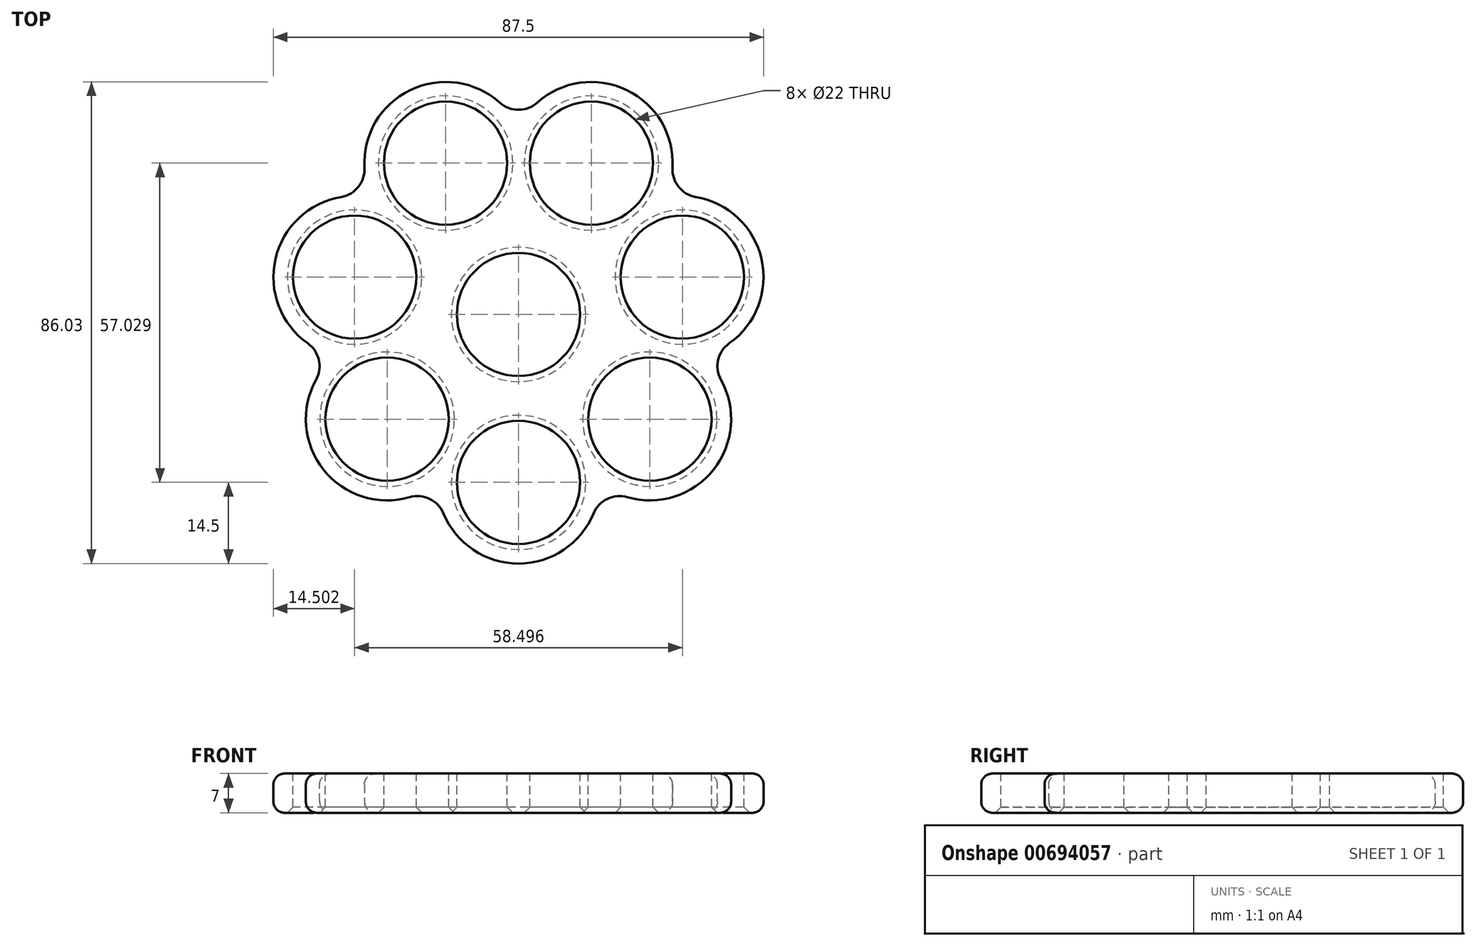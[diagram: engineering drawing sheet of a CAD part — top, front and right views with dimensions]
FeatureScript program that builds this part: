
annotation { "Feature Type Name" : "Feature", "Feature Type Description" : "" }
export const myFeature = defineFeature(function(context is Context, id is Id, definition is map)
    precondition{}
    {
        {
            var Q0;
            Q0=qCreatedBy(makeId("Top.planeOp"),FACE);
            var sketch = newSketch(context, id + "F0", { "sketchPlane" : qUnion([Q0])});
            skCircle(sketch, "E0", {"center": v(0, 0) * mm, "radius": 14.5 * mm});
            skCircle(sketch, "E1", {"center": v(0, -30) * mm, "radius": 14.5 * mm});
            skLineSegment(sketch, "E2", {"start": v(14.5, 0) * mm, "end": v(14.5, -30) * mm});
            skLineSegment(sketch, "E3", {"start": v(-14.5, 0) * mm, "end": v(-14.5, -30) * mm});
            skSolve(sketch);
        }
        {
            var Q0;
            Q0=qSketchRegion(id+"F0",true);
            var Q1;
            {var subQ0=sQuery(id+"F0.wireOp",EDGE,"E1");var subQ1=sQuery(id+"F0.wireOp",EDGE,"E0");var subQ2=makeQuery(id+"F0.imprint","INTERSECT",VERTEX,{"disambiguationData":[OD(0.0)],"derivedFrom":[subQ1,subQ0]});Q1=makeQuery(id+"F0.imprint","IMPRINT",FACE,{"disambiguationData":[TD([[makeQuery(id+"F0.imprint","IMPRINT",EDGE,{"disambiguationData":[TD([[subQ2,-1.0]])],"derivedFrom":subQ1}),1.0]])]});}
            extrude(context, id + "F1", {"entities" : qUnion([Q0, Q1]), "depth" : 7 * mm, "offsetDistance" : 25 * mm});
        }
        {
            var Q0;
            Q0=qCreatedBy(makeId("Front.planeOp"),FACE);
            var sketch = newSketch(context, id + "F2", { "sketchPlane" : qUnion([Q0])});
            skLineSegment(sketch, "E4", {"start": v(0, 0) * mm, "end": v(0, 26.48) * mm});
            skSolve(sketch);
        }
        {
            var Q0;
            Q0=makeQuery(id+"F1.opExtrude","SWEPT_BODY",BODY,{"disambiguationData":[OSD([sQuery(id+"F0.wireOp",EDGE,"E0"),sQuery(id+"F0.wireOp",EDGE,"E1"),sQuery(id+"F0.wireOp",EDGE,"E2"),sQuery(id+"F0.wireOp",EDGE,"E3")])]});
            var Q1;
            Q1=sQuery(id+"F2.wireOp",EDGE,"E4");
            circularPattern(context, id + "F3", {"entities" : qUnion([Q0]), "axis" : qUnion([Q1]), "angle" : 360 * degree, "instanceCount" : 7, "equalSpace" : true});
        }
        {
            var Q0;
            Q0=makeQuery(id+"F3.opPattern","COPY",BODY,{"derivedFrom":makeQuery(id+"F1.opExtrude","SWEPT_BODY",BODY,{"disambiguationData":[OSD([sQuery(id+"F0.wireOp",EDGE,"E0"),sQuery(id+"F0.wireOp",EDGE,"E1"),sQuery(id+"F0.wireOp",EDGE,"E2"),sQuery(id+"F0.wireOp",EDGE,"E3")])]}),"instanceName":"5"});
            var Q1;
            Q1=makeQuery(id+"F3.opPattern","COPY",BODY,{"derivedFrom":makeQuery(id+"F1.opExtrude","SWEPT_BODY",BODY,{"disambiguationData":[OSD([sQuery(id+"F0.wireOp",EDGE,"E0"),sQuery(id+"F0.wireOp",EDGE,"E1"),sQuery(id+"F0.wireOp",EDGE,"E2"),sQuery(id+"F0.wireOp",EDGE,"E3")])]}),"instanceName":"6"});
            var Q2;
            Q2=makeQuery(id+"F1.opExtrude","SWEPT_BODY",BODY,{"disambiguationData":[OSD([sQuery(id+"F0.wireOp",EDGE,"E0"),sQuery(id+"F0.wireOp",EDGE,"E1"),sQuery(id+"F0.wireOp",EDGE,"E2"),sQuery(id+"F0.wireOp",EDGE,"E3")])]});
            var Q3;
            Q3=makeQuery(id+"F3.opPattern","COPY",BODY,{"derivedFrom":makeQuery(id+"F1.opExtrude","SWEPT_BODY",BODY,{"disambiguationData":[OSD([sQuery(id+"F0.wireOp",EDGE,"E0"),sQuery(id+"F0.wireOp",EDGE,"E1"),sQuery(id+"F0.wireOp",EDGE,"E2"),sQuery(id+"F0.wireOp",EDGE,"E3")])]}),"instanceName":"1"});
            var Q4;
            Q4=makeQuery(id+"F3.opPattern","COPY",BODY,{"derivedFrom":makeQuery(id+"F1.opExtrude","SWEPT_BODY",BODY,{"disambiguationData":[OSD([sQuery(id+"F0.wireOp",EDGE,"E0"),sQuery(id+"F0.wireOp",EDGE,"E1"),sQuery(id+"F0.wireOp",EDGE,"E2"),sQuery(id+"F0.wireOp",EDGE,"E3")])]}),"instanceName":"2"});
            var Q5;
            Q5=makeQuery(id+"F3.opPattern","COPY",BODY,{"derivedFrom":makeQuery(id+"F1.opExtrude","SWEPT_BODY",BODY,{"disambiguationData":[OSD([sQuery(id+"F0.wireOp",EDGE,"E0"),sQuery(id+"F0.wireOp",EDGE,"E1"),sQuery(id+"F0.wireOp",EDGE,"E2"),sQuery(id+"F0.wireOp",EDGE,"E3")])]}),"instanceName":"3"});
            var Q6;
            Q6=makeQuery(id+"F3.opPattern","COPY",BODY,{"derivedFrom":makeQuery(id+"F1.opExtrude","SWEPT_BODY",BODY,{"disambiguationData":[OSD([sQuery(id+"F0.wireOp",EDGE,"E0"),sQuery(id+"F0.wireOp",EDGE,"E1"),sQuery(id+"F0.wireOp",EDGE,"E2"),sQuery(id+"F0.wireOp",EDGE,"E3")])]}),"instanceName":"4"});
            booleanBodies(context, id + "F4", {"operationType" : BooleanOperationType.UNION, "tools" : qUnion([Q0, Q1, Q2, Q3, Q4, Q5, Q6])});
        }
        {
            var Q0;
            Q0=makeQuery(id+"F1.opExtrude","CAP_FACE",FACE,{"disambiguationData":[OSD([sQuery(id+"F0.wireOp",EDGE,"E0"),sQuery(id+"F0.wireOp",EDGE,"E1"),sQuery(id+"F0.wireOp",EDGE,"E2"),sQuery(id+"F0.wireOp",EDGE,"E3")])],"isStart":false});
            var sketch = newSketch(context, id + "F5", { "sketchPlane" : qUnion([Q0])});
            skCircle(sketch, "E5", {"center": v(0, 0) * mm, "radius": 11 * mm});
            skCircle(sketch, "E6", {"center": v(0, -30) * mm, "radius": 11 * mm});
            skLineSegment(sketch, "E7", {"start": v(0, 0) * mm, "end": v(0, -30) * mm});
            skCircle(sketch, "E8.1.0", {"center": v(23.45, -18.7) * mm, "radius": 11 * mm});
            skCircle(sketch, "E8.2.0", {"center": v(29.25, 6.68) * mm, "radius": 11 * mm});
            skCircle(sketch, "E8.3.0", {"center": v(13.02, 27.03) * mm, "radius": 11 * mm});
            skCircle(sketch, "E8.4.0", {"center": v(-13.02, 27.03) * mm, "radius": 11 * mm});
            skCircle(sketch, "E8.5.0", {"center": v(-29.25, 6.68) * mm, "radius": 11 * mm});
            skCircle(sketch, "E8.6.0", {"center": v(-23.45, -18.7) * mm, "radius": 11 * mm});
            skSolve(sketch);
        }
        {
            var Q0;
            Q0=qSketchRegion(id+"F5",true);
            extrude(context, id + "F6", {"entities" : qUnion([Q0]), "operationType" : NewBodyOperationType.REMOVE, "endBound" : BoundingType.THROUGH_ALL, "oppositeDirection" : true, "depth" : 25 * mm, "offsetDistance" : 25 * mm});
        }
        {
            var Q0;
            {var subQ0=makeQuery(id+"F1.opExtrude","SWEPT_FACE",FACE,{"disambiguationData":[OSD([sQuery(id+"F0.wireOp",EDGE,"E1")])]});Q0=makeQuery(id+"F4.opBoolean","INTERSECT",EDGE,{"derivedFrom":[makeQuery(id+"F3.opPattern","COPY",FACE,{"derivedFrom":subQ0,"instanceName":"4"}),makeQuery(id+"F3.opPattern","COPY",FACE,{"derivedFrom":subQ0,"instanceName":"5"})]});}
            var Q1;
            {var subQ0=makeQuery(id+"F1.opExtrude","SWEPT_FACE",FACE,{"disambiguationData":[OSD([sQuery(id+"F0.wireOp",EDGE,"E1")])]});Q1=makeQuery(id+"F4.opBoolean","INTERSECT",EDGE,{"derivedFrom":[makeQuery(id+"F3.opPattern","COPY",FACE,{"derivedFrom":subQ0,"instanceName":"5"}),makeQuery(id+"F3.opPattern","COPY",FACE,{"derivedFrom":subQ0,"instanceName":"6"})]});}
            var Q2;
            {var subQ0=makeQuery(id+"F1.opExtrude","SWEPT_FACE",FACE,{"disambiguationData":[OSD([sQuery(id+"F0.wireOp",EDGE,"E1")])]});Q2=makeQuery(id+"F4.opBoolean","INTERSECT",EDGE,{"derivedFrom":[subQ0,makeQuery(id+"F3.opPattern","COPY",FACE,{"derivedFrom":subQ0,"instanceName":"6"})]});}
            var Q3;
            {var subQ0=makeQuery(id+"F1.opExtrude","SWEPT_FACE",FACE,{"disambiguationData":[OSD([sQuery(id+"F0.wireOp",EDGE,"E1")])]});Q3=makeQuery(id+"F4.opBoolean","INTERSECT",EDGE,{"derivedFrom":[subQ0,makeQuery(id+"F3.opPattern","COPY",FACE,{"derivedFrom":subQ0,"instanceName":"1"})]});}
            var Q4;
            {var subQ0=makeQuery(id+"F1.opExtrude","SWEPT_FACE",FACE,{"disambiguationData":[OSD([sQuery(id+"F0.wireOp",EDGE,"E1")])]});Q4=makeQuery(id+"F4.opBoolean","INTERSECT",EDGE,{"derivedFrom":[makeQuery(id+"F3.opPattern","COPY",FACE,{"derivedFrom":subQ0,"instanceName":"1"}),makeQuery(id+"F3.opPattern","COPY",FACE,{"derivedFrom":subQ0,"instanceName":"2"})]});}
            var Q5;
            {var subQ0=makeQuery(id+"F1.opExtrude","SWEPT_FACE",FACE,{"disambiguationData":[OSD([sQuery(id+"F0.wireOp",EDGE,"E1")])]});Q5=makeQuery(id+"F4.opBoolean","INTERSECT",EDGE,{"derivedFrom":[makeQuery(id+"F3.opPattern","COPY",FACE,{"derivedFrom":subQ0,"instanceName":"2"}),makeQuery(id+"F3.opPattern","COPY",FACE,{"derivedFrom":subQ0,"instanceName":"3"})]});}
            var Q6;
            {var subQ0=makeQuery(id+"F1.opExtrude","SWEPT_FACE",FACE,{"disambiguationData":[OSD([sQuery(id+"F0.wireOp",EDGE,"E1")])]});Q6=makeQuery(id+"F4.opBoolean","INTERSECT",EDGE,{"derivedFrom":[makeQuery(id+"F3.opPattern","COPY",FACE,{"derivedFrom":subQ0,"instanceName":"3"}),makeQuery(id+"F3.opPattern","COPY",FACE,{"derivedFrom":subQ0,"instanceName":"4"})]});}
            fillet(context, id + "F7", {"entities" : qUnion([Q0, Q1, Q2, Q3, Q4, Q5, Q6]), "radius" : 5 * mm, "tangentPropagation" : true, "allowEdgeOverflow" : false});
        }
        {
            var Q0;
            Q0=makeQuery(id+"F3.opPattern","COPY",EDGE,{"derivedFrom":makeQuery(id+"F1.opExtrude","CAP_EDGE",EDGE,{"disambiguationData":[OSD([sQuery(id+"F0.wireOp",EDGE,"E1")])],"isStart":false}),"instanceName":"1"});
            var Q1;
            Q1=makeQuery(id+"F1.opExtrude","CAP_EDGE",EDGE,{"disambiguationData":[OSD([sQuery(id+"F0.wireOp",EDGE,"E1")])],"isStart":true});
            fillet(context, id + "F8", {"entities" : qUnion([Q0, Q1]), "radius" : 2 * mm, "tangentPropagation" : true, "allowEdgeOverflow" : false});
        }
        {
            var Q0;
            Q0=makeQuery(id+"F3.opPattern","COPY",EDGE,{"derivedFrom":makeQuery(id+"F6.boolean.opBoolean","COPY",EDGE,{"derivedFrom":makeQuery(id+"F6.opExtrude","CAP_EDGE",EDGE,{"disambiguationData":[OSD([sQuery(id+"F5.wireOp",EDGE,"E5")])],"isStart":true})}),"instanceName":"4"});
            var Q1;
            Q1=makeQuery(id+"F3.opPattern","COPY",EDGE,{"derivedFrom":makeQuery(id+"F6.boolean.opBoolean","COPY",EDGE,{"derivedFrom":makeQuery(id+"F6.opExtrude","CAP_EDGE",EDGE,{"disambiguationData":[OSD([sQuery(id+"F5.wireOp",EDGE,"E6")])],"isStart":true})}),"instanceName":"2"});
            var Q2;
            Q2=makeQuery(id+"F3.opPattern","COPY",EDGE,{"derivedFrom":makeQuery(id+"F6.boolean.opBoolean","COPY",EDGE,{"derivedFrom":makeQuery(id+"F6.opExtrude","CAP_EDGE",EDGE,{"disambiguationData":[OSD([sQuery(id+"F5.wireOp",EDGE,"E6")])],"isStart":true})}),"instanceName":"3"});
            var Q3;
            Q3=makeQuery(id+"F3.opPattern","COPY",EDGE,{"derivedFrom":makeQuery(id+"F6.boolean.opBoolean","COPY",EDGE,{"derivedFrom":makeQuery(id+"F6.opExtrude","CAP_EDGE",EDGE,{"disambiguationData":[OSD([sQuery(id+"F5.wireOp",EDGE,"E6")])],"isStart":true})}),"instanceName":"4"});
            var Q4;
            Q4=makeQuery(id+"F3.opPattern","COPY",EDGE,{"derivedFrom":makeQuery(id+"F6.boolean.opBoolean","COPY",EDGE,{"derivedFrom":makeQuery(id+"F6.opExtrude","CAP_EDGE",EDGE,{"disambiguationData":[OSD([sQuery(id+"F5.wireOp",EDGE,"E6")])],"isStart":true})}),"instanceName":"5"});
            var Q5;
            Q5=makeQuery(id+"F6.boolean.opBoolean","COPY",EDGE,{"derivedFrom":makeQuery(id+"F6.opExtrude","CAP_EDGE",EDGE,{"disambiguationData":[OSD([sQuery(id+"F5.wireOp",EDGE,"E6")])],"isStart":true})});
            var Q6;
            Q6=makeQuery(id+"F3.opPattern","COPY",EDGE,{"derivedFrom":makeQuery(id+"F6.boolean.opBoolean","COPY",EDGE,{"derivedFrom":makeQuery(id+"F6.opExtrude","CAP_EDGE",EDGE,{"disambiguationData":[OSD([sQuery(id+"F5.wireOp",EDGE,"E6")])],"isStart":true})}),"instanceName":"1"});
            var Q7;
            Q7=makeQuery(id+"F3.opPattern","COPY",EDGE,{"derivedFrom":makeQuery(id+"F6.boolean.opBoolean","INTERSECT",EDGE,{"derivedFrom":[makeQuery(id+"F1.opExtrude","CAP_FACE",FACE,{"disambiguationData":[OSD([sQuery(id+"F0.wireOp",EDGE,"E0"),sQuery(id+"F0.wireOp",EDGE,"E1"),sQuery(id+"F0.wireOp",EDGE,"E2"),sQuery(id+"F0.wireOp",EDGE,"E3")])],"isStart":true}),makeQuery(id+"F6.opExtrude","SWEPT_FACE",FACE,{"disambiguationData":[OSD([sQuery(id+"F5.wireOp",EDGE,"E6")])]})]}),"instanceName":"5"});
            var Q8;
            Q8=makeQuery(id+"F6.boolean.opBoolean","INTERSECT",EDGE,{"derivedFrom":[makeQuery(id+"F1.opExtrude","CAP_FACE",FACE,{"disambiguationData":[OSD([sQuery(id+"F0.wireOp",EDGE,"E0"),sQuery(id+"F0.wireOp",EDGE,"E1"),sQuery(id+"F0.wireOp",EDGE,"E2"),sQuery(id+"F0.wireOp",EDGE,"E3")])],"isStart":true}),makeQuery(id+"F6.opExtrude","SWEPT_FACE",FACE,{"disambiguationData":[OSD([sQuery(id+"F5.wireOp",EDGE,"E6")])]})]});
            var Q9;
            Q9=makeQuery(id+"F3.opPattern","COPY",EDGE,{"derivedFrom":makeQuery(id+"F6.boolean.opBoolean","INTERSECT",EDGE,{"derivedFrom":[makeQuery(id+"F1.opExtrude","CAP_FACE",FACE,{"disambiguationData":[OSD([sQuery(id+"F0.wireOp",EDGE,"E0"),sQuery(id+"F0.wireOp",EDGE,"E1"),sQuery(id+"F0.wireOp",EDGE,"E2"),sQuery(id+"F0.wireOp",EDGE,"E3")])],"isStart":true}),makeQuery(id+"F6.opExtrude","SWEPT_FACE",FACE,{"disambiguationData":[OSD([sQuery(id+"F5.wireOp",EDGE,"E6")])]})]}),"instanceName":"1"});
            var Q10;
            Q10=makeQuery(id+"F3.opPattern","COPY",EDGE,{"derivedFrom":makeQuery(id+"F6.boolean.opBoolean","INTERSECT",EDGE,{"derivedFrom":[makeQuery(id+"F1.opExtrude","CAP_FACE",FACE,{"disambiguationData":[OSD([sQuery(id+"F0.wireOp",EDGE,"E0"),sQuery(id+"F0.wireOp",EDGE,"E1"),sQuery(id+"F0.wireOp",EDGE,"E2"),sQuery(id+"F0.wireOp",EDGE,"E3")])],"isStart":true}),makeQuery(id+"F6.opExtrude","SWEPT_FACE",FACE,{"disambiguationData":[OSD([sQuery(id+"F5.wireOp",EDGE,"E6")])]})]}),"instanceName":"2"});
            var Q11;
            Q11=makeQuery(id+"F3.opPattern","COPY",EDGE,{"derivedFrom":makeQuery(id+"F6.boolean.opBoolean","INTERSECT",EDGE,{"derivedFrom":[makeQuery(id+"F1.opExtrude","CAP_FACE",FACE,{"disambiguationData":[OSD([sQuery(id+"F0.wireOp",EDGE,"E0"),sQuery(id+"F0.wireOp",EDGE,"E1"),sQuery(id+"F0.wireOp",EDGE,"E2"),sQuery(id+"F0.wireOp",EDGE,"E3")])],"isStart":true}),makeQuery(id+"F6.opExtrude","SWEPT_FACE",FACE,{"disambiguationData":[OSD([sQuery(id+"F5.wireOp",EDGE,"E6")])]})]}),"instanceName":"3"});
            var Q12;
            Q12=makeQuery(id+"F3.opPattern","COPY",EDGE,{"derivedFrom":makeQuery(id+"F6.boolean.opBoolean","INTERSECT",EDGE,{"derivedFrom":[makeQuery(id+"F1.opExtrude","CAP_FACE",FACE,{"disambiguationData":[OSD([sQuery(id+"F0.wireOp",EDGE,"E0"),sQuery(id+"F0.wireOp",EDGE,"E1"),sQuery(id+"F0.wireOp",EDGE,"E2"),sQuery(id+"F0.wireOp",EDGE,"E3")])],"isStart":true}),makeQuery(id+"F6.opExtrude","SWEPT_FACE",FACE,{"disambiguationData":[OSD([sQuery(id+"F5.wireOp",EDGE,"E5")])]})]}),"instanceName":"4"});
            var Q13;
            Q13=makeQuery(id+"F3.opPattern","COPY",EDGE,{"derivedFrom":makeQuery(id+"F6.boolean.opBoolean","INTERSECT",EDGE,{"derivedFrom":[makeQuery(id+"F1.opExtrude","CAP_FACE",FACE,{"disambiguationData":[OSD([sQuery(id+"F0.wireOp",EDGE,"E0"),sQuery(id+"F0.wireOp",EDGE,"E1"),sQuery(id+"F0.wireOp",EDGE,"E2"),sQuery(id+"F0.wireOp",EDGE,"E3")])],"isStart":true}),makeQuery(id+"F6.opExtrude","SWEPT_FACE",FACE,{"disambiguationData":[OSD([sQuery(id+"F5.wireOp",EDGE,"E6")])]})]}),"instanceName":"4"});
            var Q14;
            Q14=makeQuery(id+"F6.boolean.opBoolean","COPY",EDGE,{"derivedFrom":makeQuery(id+"F6.opExtrude","CAP_EDGE",EDGE,{"disambiguationData":[OSD([sQuery(id+"F5.wireOp",EDGE,"E8.6.0")])],"isStart":true})});
            var Q15;
            Q15=makeQuery(id+"F6.boolean.opBoolean","COPY",EDGE,{"derivedFrom":makeQuery(id+"F6.opExtrude","CAP_EDGE",EDGE,{"disambiguationData":[OSD([sQuery(id+"F5.wireOp",EDGE,"E8.5.0")])],"isStart":true})});
            var Q16;
            Q16=makeQuery(id+"F6.boolean.opBoolean","COPY",EDGE,{"derivedFrom":makeQuery(id+"F6.opExtrude","CAP_EDGE",EDGE,{"disambiguationData":[OSD([sQuery(id+"F5.wireOp",EDGE,"E8.4.0")])],"isStart":true})});
            var Q17;
            Q17=makeQuery(id+"F6.boolean.opBoolean","COPY",EDGE,{"derivedFrom":makeQuery(id+"F6.opExtrude","CAP_EDGE",EDGE,{"disambiguationData":[OSD([sQuery(id+"F5.wireOp",EDGE,"E8.3.0")])],"isStart":true})});
            var Q18;
            Q18=makeQuery(id+"F6.boolean.opBoolean","COPY",EDGE,{"derivedFrom":makeQuery(id+"F6.opExtrude","CAP_EDGE",EDGE,{"disambiguationData":[OSD([sQuery(id+"F5.wireOp",EDGE,"E5")])],"isStart":true})});
            var Q19;
            Q19=makeQuery(id+"F6.boolean.opBoolean","COPY",EDGE,{"derivedFrom":makeQuery(id+"F6.opExtrude","CAP_EDGE",EDGE,{"disambiguationData":[OSD([sQuery(id+"F5.wireOp",EDGE,"E8.2.0")])],"isStart":true})});
            var Q20;
            Q20=makeQuery(id+"F6.boolean.opBoolean","COPY",EDGE,{"derivedFrom":makeQuery(id+"F6.opExtrude","CAP_EDGE",EDGE,{"disambiguationData":[OSD([sQuery(id+"F5.wireOp",EDGE,"E8.1.0")])],"isStart":true})});
            var Q21;
            {var subQ0=makeQuery(id+"F1.opExtrude","CAP_FACE",FACE,{"disambiguationData":[OSD([sQuery(id+"F0.wireOp",EDGE,"E0"),sQuery(id+"F0.wireOp",EDGE,"E1"),sQuery(id+"F0.wireOp",EDGE,"E2"),sQuery(id+"F0.wireOp",EDGE,"E3")])],"isStart":true});Q21=makeQuery(id+"F6.boolean.opBoolean","INTERSECT",EDGE,{"derivedFrom":[makeQuery(id+"F4.opBoolean","MERGE",FACE,{"derivedFrom":[subQ0,makeQuery(id+"F3.opPattern","COPY",FACE,{"derivedFrom":subQ0,"instanceName":"1"}),makeQuery(id+"F3.opPattern","COPY",FACE,{"derivedFrom":subQ0,"instanceName":"2"}),makeQuery(id+"F3.opPattern","COPY",FACE,{"derivedFrom":subQ0,"instanceName":"3"}),makeQuery(id+"F3.opPattern","COPY",FACE,{"derivedFrom":subQ0,"instanceName":"4"}),makeQuery(id+"F3.opPattern","COPY",FACE,{"derivedFrom":subQ0,"instanceName":"5"}),makeQuery(id+"F3.opPattern","COPY",FACE,{"derivedFrom":subQ0,"instanceName":"6"})]}),makeQuery(id+"F6.opExtrude","SWEPT_FACE",FACE,{"disambiguationData":[OSD([sQuery(id+"F5.wireOp",EDGE,"E8.2.0")])]})]});}
            var Q22;
            {var subQ0=makeQuery(id+"F1.opExtrude","CAP_FACE",FACE,{"disambiguationData":[OSD([sQuery(id+"F0.wireOp",EDGE,"E0"),sQuery(id+"F0.wireOp",EDGE,"E1"),sQuery(id+"F0.wireOp",EDGE,"E2"),sQuery(id+"F0.wireOp",EDGE,"E3")])],"isStart":true});Q22=makeQuery(id+"F6.boolean.opBoolean","INTERSECT",EDGE,{"derivedFrom":[makeQuery(id+"F4.opBoolean","MERGE",FACE,{"derivedFrom":[subQ0,makeQuery(id+"F3.opPattern","COPY",FACE,{"derivedFrom":subQ0,"instanceName":"1"}),makeQuery(id+"F3.opPattern","COPY",FACE,{"derivedFrom":subQ0,"instanceName":"2"}),makeQuery(id+"F3.opPattern","COPY",FACE,{"derivedFrom":subQ0,"instanceName":"3"}),makeQuery(id+"F3.opPattern","COPY",FACE,{"derivedFrom":subQ0,"instanceName":"4"}),makeQuery(id+"F3.opPattern","COPY",FACE,{"derivedFrom":subQ0,"instanceName":"5"}),makeQuery(id+"F3.opPattern","COPY",FACE,{"derivedFrom":subQ0,"instanceName":"6"})]}),makeQuery(id+"F6.opExtrude","SWEPT_FACE",FACE,{"disambiguationData":[OSD([sQuery(id+"F5.wireOp",EDGE,"E8.1.0")])]})]});}
            var Q23;
            {var subQ0=makeQuery(id+"F1.opExtrude","CAP_FACE",FACE,{"disambiguationData":[OSD([sQuery(id+"F0.wireOp",EDGE,"E0"),sQuery(id+"F0.wireOp",EDGE,"E1"),sQuery(id+"F0.wireOp",EDGE,"E2"),sQuery(id+"F0.wireOp",EDGE,"E3")])],"isStart":true});Q23=makeQuery(id+"F6.boolean.opBoolean","INTERSECT",EDGE,{"derivedFrom":[makeQuery(id+"F4.opBoolean","MERGE",FACE,{"derivedFrom":[subQ0,makeQuery(id+"F3.opPattern","COPY",FACE,{"derivedFrom":subQ0,"instanceName":"1"}),makeQuery(id+"F3.opPattern","COPY",FACE,{"derivedFrom":subQ0,"instanceName":"2"}),makeQuery(id+"F3.opPattern","COPY",FACE,{"derivedFrom":subQ0,"instanceName":"3"}),makeQuery(id+"F3.opPattern","COPY",FACE,{"derivedFrom":subQ0,"instanceName":"4"}),makeQuery(id+"F3.opPattern","COPY",FACE,{"derivedFrom":subQ0,"instanceName":"5"}),makeQuery(id+"F3.opPattern","COPY",FACE,{"derivedFrom":subQ0,"instanceName":"6"})]}),makeQuery(id+"F6.opExtrude","SWEPT_FACE",FACE,{"disambiguationData":[OSD([sQuery(id+"F5.wireOp",EDGE,"E8.6.0")])]})]});}
            var Q24;
            {var subQ0=makeQuery(id+"F1.opExtrude","CAP_FACE",FACE,{"disambiguationData":[OSD([sQuery(id+"F0.wireOp",EDGE,"E0"),sQuery(id+"F0.wireOp",EDGE,"E1"),sQuery(id+"F0.wireOp",EDGE,"E2"),sQuery(id+"F0.wireOp",EDGE,"E3")])],"isStart":true});Q24=makeQuery(id+"F6.boolean.opBoolean","INTERSECT",EDGE,{"derivedFrom":[makeQuery(id+"F4.opBoolean","MERGE",FACE,{"derivedFrom":[subQ0,makeQuery(id+"F3.opPattern","COPY",FACE,{"derivedFrom":subQ0,"instanceName":"1"}),makeQuery(id+"F3.opPattern","COPY",FACE,{"derivedFrom":subQ0,"instanceName":"2"}),makeQuery(id+"F3.opPattern","COPY",FACE,{"derivedFrom":subQ0,"instanceName":"3"}),makeQuery(id+"F3.opPattern","COPY",FACE,{"derivedFrom":subQ0,"instanceName":"4"}),makeQuery(id+"F3.opPattern","COPY",FACE,{"derivedFrom":subQ0,"instanceName":"5"}),makeQuery(id+"F3.opPattern","COPY",FACE,{"derivedFrom":subQ0,"instanceName":"6"})]}),makeQuery(id+"F6.opExtrude","SWEPT_FACE",FACE,{"disambiguationData":[OSD([sQuery(id+"F5.wireOp",EDGE,"E8.5.0")])]})]});}
            var Q25;
            {var subQ0=makeQuery(id+"F1.opExtrude","CAP_FACE",FACE,{"disambiguationData":[OSD([sQuery(id+"F0.wireOp",EDGE,"E0"),sQuery(id+"F0.wireOp",EDGE,"E1"),sQuery(id+"F0.wireOp",EDGE,"E2"),sQuery(id+"F0.wireOp",EDGE,"E3")])],"isStart":true});Q25=makeQuery(id+"F6.boolean.opBoolean","INTERSECT",EDGE,{"derivedFrom":[makeQuery(id+"F4.opBoolean","MERGE",FACE,{"derivedFrom":[subQ0,makeQuery(id+"F3.opPattern","COPY",FACE,{"derivedFrom":subQ0,"instanceName":"1"}),makeQuery(id+"F3.opPattern","COPY",FACE,{"derivedFrom":subQ0,"instanceName":"2"}),makeQuery(id+"F3.opPattern","COPY",FACE,{"derivedFrom":subQ0,"instanceName":"3"}),makeQuery(id+"F3.opPattern","COPY",FACE,{"derivedFrom":subQ0,"instanceName":"4"}),makeQuery(id+"F3.opPattern","COPY",FACE,{"derivedFrom":subQ0,"instanceName":"5"}),makeQuery(id+"F3.opPattern","COPY",FACE,{"derivedFrom":subQ0,"instanceName":"6"})]}),makeQuery(id+"F6.opExtrude","SWEPT_FACE",FACE,{"disambiguationData":[OSD([sQuery(id+"F5.wireOp",EDGE,"E8.4.0")])]})]});}
            var Q26;
            {var subQ0=makeQuery(id+"F1.opExtrude","CAP_FACE",FACE,{"disambiguationData":[OSD([sQuery(id+"F0.wireOp",EDGE,"E0"),sQuery(id+"F0.wireOp",EDGE,"E1"),sQuery(id+"F0.wireOp",EDGE,"E2"),sQuery(id+"F0.wireOp",EDGE,"E3")])],"isStart":true});Q26=makeQuery(id+"F6.boolean.opBoolean","INTERSECT",EDGE,{"derivedFrom":[makeQuery(id+"F4.opBoolean","MERGE",FACE,{"derivedFrom":[subQ0,makeQuery(id+"F3.opPattern","COPY",FACE,{"derivedFrom":subQ0,"instanceName":"1"}),makeQuery(id+"F3.opPattern","COPY",FACE,{"derivedFrom":subQ0,"instanceName":"2"}),makeQuery(id+"F3.opPattern","COPY",FACE,{"derivedFrom":subQ0,"instanceName":"3"}),makeQuery(id+"F3.opPattern","COPY",FACE,{"derivedFrom":subQ0,"instanceName":"4"}),makeQuery(id+"F3.opPattern","COPY",FACE,{"derivedFrom":subQ0,"instanceName":"5"}),makeQuery(id+"F3.opPattern","COPY",FACE,{"derivedFrom":subQ0,"instanceName":"6"})]}),makeQuery(id+"F6.opExtrude","SWEPT_FACE",FACE,{"disambiguationData":[OSD([sQuery(id+"F5.wireOp",EDGE,"E8.3.0")])]})]});}
            var Q27;
            {var subQ0=makeQuery(id+"F1.opExtrude","CAP_FACE",FACE,{"disambiguationData":[OSD([sQuery(id+"F0.wireOp",EDGE,"E0"),sQuery(id+"F0.wireOp",EDGE,"E1"),sQuery(id+"F0.wireOp",EDGE,"E2"),sQuery(id+"F0.wireOp",EDGE,"E3")])],"isStart":true});Q27=makeQuery(id+"F6.boolean.opBoolean","INTERSECT",EDGE,{"derivedFrom":[makeQuery(id+"F4.opBoolean","MERGE",FACE,{"derivedFrom":[subQ0,makeQuery(id+"F3.opPattern","COPY",FACE,{"derivedFrom":subQ0,"instanceName":"1"}),makeQuery(id+"F3.opPattern","COPY",FACE,{"derivedFrom":subQ0,"instanceName":"2"}),makeQuery(id+"F3.opPattern","COPY",FACE,{"derivedFrom":subQ0,"instanceName":"3"}),makeQuery(id+"F3.opPattern","COPY",FACE,{"derivedFrom":subQ0,"instanceName":"4"}),makeQuery(id+"F3.opPattern","COPY",FACE,{"derivedFrom":subQ0,"instanceName":"5"}),makeQuery(id+"F3.opPattern","COPY",FACE,{"derivedFrom":subQ0,"instanceName":"6"})]}),makeQuery(id+"F6.opExtrude","SWEPT_FACE",FACE,{"disambiguationData":[OSD([sQuery(id+"F5.wireOp",EDGE,"E5")])]})]});}
            chamfer(context, id + "F9", {"entities" : qUnion([Q0, Q1, Q2, Q3, Q4, Q5, Q6, Q7, Q8, Q9, Q10, Q11, Q12, Q13, Q14, Q15, Q16, Q17, Q18, Q19, Q20, Q21, Q22, Q23, Q24, Q25, Q26, Q27]), "width" : 1 * mm, "tangentPropagation" : true});
        }
    });
